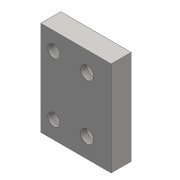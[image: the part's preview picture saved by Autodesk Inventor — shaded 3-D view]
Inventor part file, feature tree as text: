
AUTODESK INVENTOR PART (.ipt)
format: ipt  version: 2016 (Build 200138000, 138)  size: 926,208 bytes
history: native  units: mm
features: sketch x4, extrude x2, hole x2, chamfer x1, mirror x1, projected_geometry x1
ambient origin geometry x8: Origin, YZ Plane, XZ Plane, XY Plane, X Axis, Y Axis, Z Axis, Center Point
bodies: Body1 (feature_tree)
feature tree (11):
  sketch  "Sketch1"  dims[d5=4.8mm d6=4.8mm]
  extrude  "Extrusion3"  Depth=4.8mm
  chamfer  "Chamfer2"  Distance=3.0mm
  extrude  "Extrusion4"  Depth=3.0mm
  hole  "Hole1"  [1 undecoded]
  hole  "Hole3"  [1 undecoded]
  mirror  "Mirror1"
  sketch  "Sketch3"  dims[d7=3.0mm]
  sketch  "Sketch5"  dims[d8=3.0mm]
  projected_geometry  "Projected Loop1"
  sketch  "Sketch7"  dims[d9=3.0mm d10=3.0mm d11=3.0mm d12=3.0mm d17=4.25mm d19=1.5mm d20=4.3mm d21=10.0mm d22=2.0mm d23=1.5mm d24=4.3mm d25=10.0mm d26=2.0mm d35=0.5mm d37=1.5mm d48=1.0mm d52=2.0mm d53=0.0mm d54=0.2mm d55=2.0mm d56=45.0deg d60=10.0mm d63=5.0mm d64=0.0mm d65=4.0mm d66=0.0mm d67=3.2mm d68=6.0mm d69=6.0mm d70=3.5mm d71=90.0deg d72=8.0mm d73=20.594885mm d74=0.0mm d75=2.0mm d83=3.0mm d84=6.0mm d85=6.0mm d86=3.5mm d87=90.0deg d88=8.0mm d89=20.594885mm d90=0.2mm d91=0.2mm d92=0.2mm d93=0.2mm d94=0.2mm d95=0.2mm]
note: 2 required parameter values undecoded (feature->parameter linkage not recoverable at this tier; creation-order binding heuristic only, values carry confidence <= 0.55)
